# Revit family: Gira_2832600
name_source: partatom
category: Electrical Fixtures
revit_build: Autodesk Revit 2017 (Build: 20160225_1515(x64)
units: mm (PartAtom-declared; Revit-internal decimal feet)

## family parameters
Cut with Voids When Loaded = No
Host = Face
Maintain Annotation Orientation = Yes
Part Type = Normal
Room Calculation Point = No
Round Connector Dimension = Use Diameter
Shared = No

## types (1)
- Rocker sw. BS 3-g off/2-way System 55 stainl.steel(lac.)
    Assembly arrangement = Basic element with adapter plate
    Available = No
    BIM (1) = https://media.stage.bim.site und Tasten.rfa?public/gira/36a6b08/Sys55_Komplettgerät_Schalten und Tasten.rfa
    Category = Switch
    Colour = Stainless steel
    Connection type = Screwed terminal
    Data sheet (1) = https://katalog.gira.de
    Default Elevation = 1219 mm
    Description = Rock.sw.BS 3g off 2-w Sys55 SSTl,British Standard rocker switch (BS EN 60669-1) 3-gang with rockers,System 55, Support ring 71 x 71 mm, universal off 2-way switch,stainless steel (lacquered),Features:,- With screw terminals.,,Notes :,- For screw mounting only.
    GTIN = 4010337022053
    HAN = 2832600
    Halogen free = Yes
    HeinzeBIM = https://bimportal.heinze.de
    Illumination = No
    Label space/information surface = No
    Manufacturer = Gira
    Manufacturer URL = https://www.gira.de
    Material = Other
    Material quality = Other
    Method of operation = Rocker/button
    Model = Sys55_Komplettgerät_Schalten und Tasten
    Mounting method = Flush mounted (plaster)
    Name = Rocker sw. BS 3-g off/2-way System 55 stainl.steel(lac.)
    Nominal voltage = 250
    Number of modules (module system) = 1
    Number of rockers = 3
    Push button switch = No
    Rated current = 10
    Suitable for degree of protection (IP) = IP20
    Surface protection = Other
    Type of fastening = Mounting with claw and screw
    URL = http://katalog.gira.de
    Washing machine switch = No
    Wiring system = Two-way switch
    With mounting plate = No

## geometry (parser evidence)
native form markers: Sweep x9
no freeform markers — native parametric forms only
